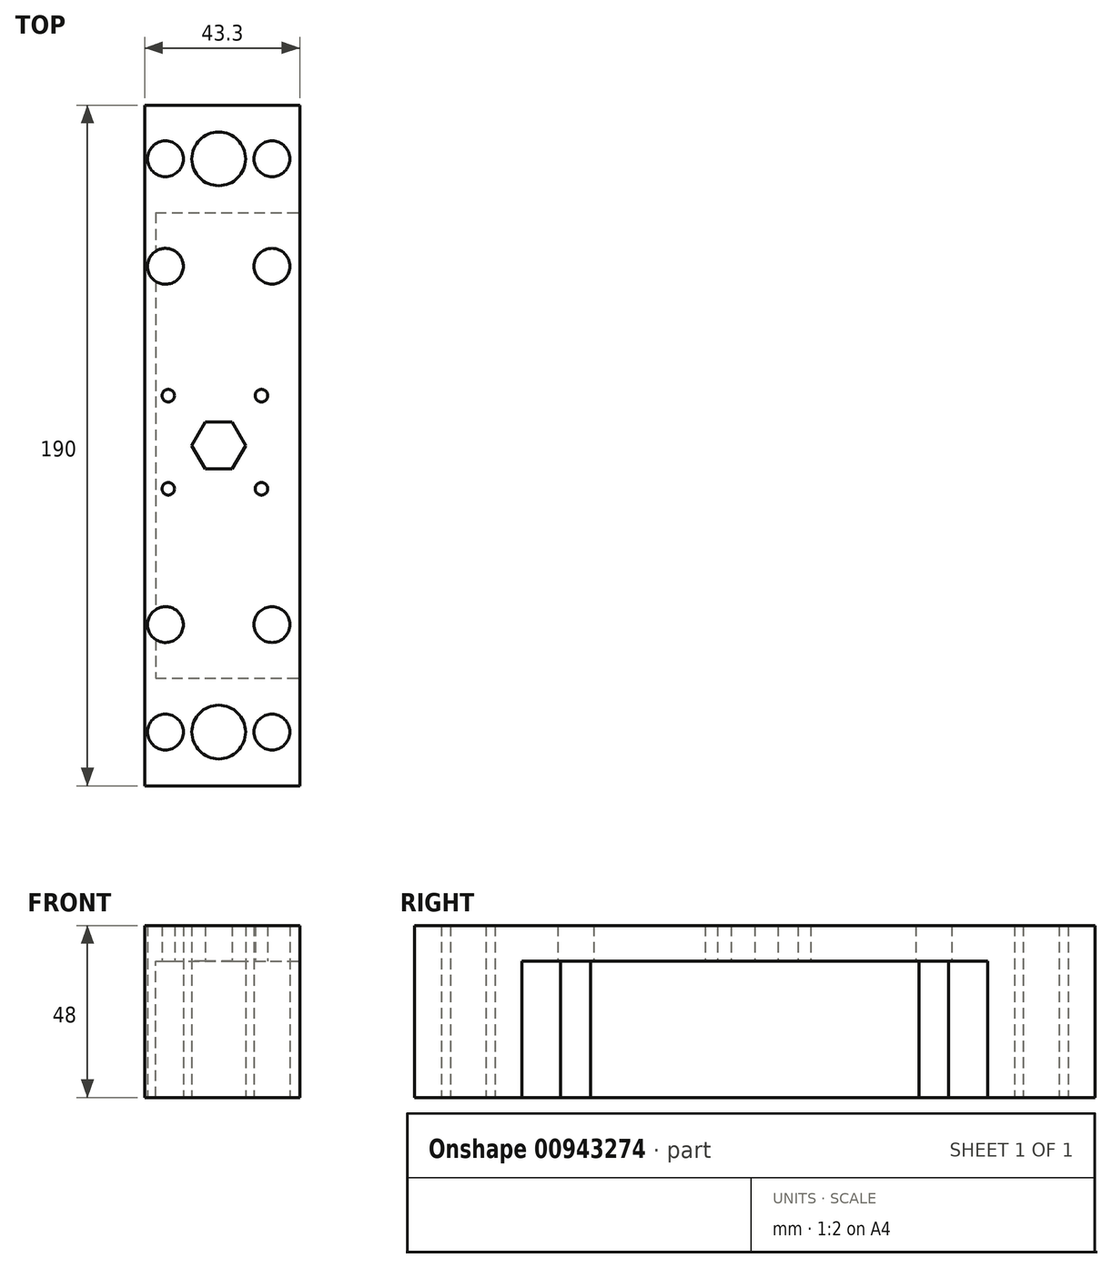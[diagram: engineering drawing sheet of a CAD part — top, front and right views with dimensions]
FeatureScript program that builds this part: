
annotation { "Feature Type Name" : "Feature", "Feature Type Description" : "" }
export const myFeature = defineFeature(function(context is Context, id is Id, definition is map)
    precondition{}
    {
        {
            var Q0;
            Q0=qCreatedBy(makeId("Top.planeOp"),FACE);
            var sketch = newSketch(context, id + "F0", { "sketchPlane" : qUnion([Q0])});
            skCircle(sketch, "E0", {"center": v(11.93, 13.9) * mm, "radius": 1.75 * mm});
            skCircle(sketch, "E1.MirrorC", {"center": v(-14.07, -12.1) * mm, "radius": 1.75 * mm});
            skCircle(sketch, "E2.MirrorC", {"center": v(11.93, -12.1) * mm, "radius": 1.75 * mm});
            skCircle(sketch, "E3.MirrorC", {"center": v(-14.07, 13.9) * mm, "radius": 1.75 * mm});
            skLineSegment(sketch, "E4", {"start": v(-20.65, 17.6) * mm, "end": v(-20.65, -17.6) * mm});
            skLineSegment(sketch, "E5", {"start": v(30.65, 0) * mm, "end": v(30.65, -95) * mm});
            skLineSegment(sketch, "E6", {"start": v(-20.65, 0) * mm, "end": v(-20.65, -95) * mm});
            skLineSegment(sketch, "E7", {"start": v(30.65, -95) * mm, "end": v(-20.65, -95) * mm});
            skLineSegment(sketch, "E8", {"start": v(0, 0) * mm, "end": v(0, -80) * mm, "construction": true});
            skCircle(sketch, "E9", {"center": v(0, -80) * mm, "radius": 7.5 * mm});
            skLineSegment(sketch, "E10.MirrorCS", {"start": v(30.65, 0) * mm, "end": v(30.65, 95) * mm});
            skLineSegment(sketch, "E11.MirrorCS", {"start": v(-20.65, 0) * mm, "end": v(-20.65, 95) * mm});
            skLineSegment(sketch, "E12.MirrorCS", {"start": v(30.65, 95) * mm, "end": v(-20.65, 95) * mm});
            skLineSegment(sketch, "E13", {"start": v(0, -80) * mm, "end": v(-20.65, -80) * mm, "construction": true});
            skCircle(sketch, "E14", {"center": v(-14.88, -80) * mm, "radius": 1.4 * mm});
            skCircle(sketch, "E15", {"center": v(-14.88, -80) * mm, "radius": 5 * mm});
            skCircle(sketch, "E16.MirrorC", {"center": v(14.88, -80) * mm, "radius": 5 * mm});
            skCircle(sketch, "E17.MirrorC", {"center": v(14.88, -80) * mm, "radius": 1.4 * mm});
            skCircle(sketch, "E18.0.1.0", {"center": v(14.88, -50) * mm, "radius": 5 * mm});
            skLineSegment(sketch, "E18.direction2", {"start": v(14.88, -80) * mm, "end": v(14.88, -50) * mm, "construction": true});
            skCircle(sketch, "E19.0.1.0", {"center": v(14.88, -50) * mm, "radius": 1.4 * mm});
            skCircle(sketch, "E20.MirrorC", {"center": v(-14.88, -50) * mm, "radius": 5 * mm});
            skCircle(sketch, "E21", {"center": v(-14.88, -50) * mm, "radius": 1.4 * mm});
            skCircle(sketch, "E22.MirrorC", {"center": v(-14.88, 50) * mm, "radius": 5 * mm});
            skCircle(sketch, "E23.MirrorC", {"center": v(-14.88, 50) * mm, "radius": 1.4 * mm});
            skCircle(sketch, "E24.MirrorC", {"center": v(14.88, 50) * mm, "radius": 5 * mm});
            skCircle(sketch, "E25.MirrorC", {"center": v(14.88, 50) * mm, "radius": 1.4 * mm});
            skCircle(sketch, "E26.MirrorC", {"center": v(14.88, 80) * mm, "radius": 5 * mm});
            skCircle(sketch, "E27.MirrorC", {"center": v(14.88, 80) * mm, "radius": 1.4 * mm});
            skCircle(sketch, "E28.MirrorC", {"center": v(0, 80) * mm, "radius": 7.5 * mm});
            skCircle(sketch, "E29.MirrorC", {"center": v(-14.88, 80) * mm, "radius": 5 * mm});
            skCircle(sketch, "E30.MirrorC", {"center": v(-14.88, 80) * mm, "radius": 1.4 * mm});
            skLineSegment(sketch, "E31", {"start": v(0, 80) * mm, "end": v(0, 0) * mm, "construction": true});
            skLineSegment(sketch, "E32", {"start": v(0, 80) * mm, "end": v(-14.88, 80) * mm, "construction": true});
            skSolve(sketch);
        }
        {
            var Q0;
            Q0=makeQuery(id+"F0.imprint","IMPRINT",FACE,{"disambiguationData":[TD([[makeQuery(id+"F0.imprint","IMPRINT",EDGE,{"derivedFrom":sQuery(id+"F0.wireOp",EDGE,"E0")}),-1.0]])]});
            var sketch = newSketch(context, id + "F1", { "sketchPlane" : qUnion([Q0])});
            skLineSegment(sketch, "E33.bottom", {"start": v(7, 10) * mm, "end": v(-7, 10) * mm});
            skLineSegment(sketch, "E33.top", {"start": v(7, -10) * mm, "end": v(-7, -10) * mm});
            skLineSegment(sketch, "E33.left", {"start": v(10, 7) * mm, "end": v(10, -7) * mm});
            skLineSegment(sketch, "E33.right", {"start": v(-10, 7) * mm, "end": v(-10, -7) * mm});
            skPoint(sketch, "E33.middle", {"position": v(0, 0) * mm});
            skCircle(sketch, "E34.cCircle", {"center": v(0, 0) * mm, "radius": 6.55 * mm, "construction": true});
            skLineSegment(sketch, "E34.0", {"start": v(-3.78, 6.55) * mm, "end": v(3.78, 6.55) * mm});
            skLineSegment(sketch, "E34.1", {"start": v(3.78, 6.55) * mm, "end": v(7.56, 0) * mm});
            skLineSegment(sketch, "E34.2", {"start": v(7.56, 0) * mm, "end": v(3.78, -6.55) * mm});
            skLineSegment(sketch, "E34.3", {"start": v(3.78, -6.55) * mm, "end": v(-3.78, -6.55) * mm});
            skLineSegment(sketch, "E34.4", {"start": v(-3.78, -6.55) * mm, "end": v(-7.56, 0) * mm});
            skLineSegment(sketch, "E34.5", {"start": v(-7.56, 0) * mm, "end": v(-3.78, 6.55) * mm});
            skPoint(sketch, "E34.0.midPoint", {"position": v(0, 6.55) * mm});
            skPoint(sketch, "E35.visualSharp", {"position": v(-10, 10) * mm});
            skArc(sketch, "E35.filletArc", {"start": v(-7, 10) * mm, "mid": v(-9.12, 9.12) * mm, "end": v(-10, 7) * mm});
            skPoint(sketch, "E36.visualSharp", {"position": v(10, 10) * mm});
            skArc(sketch, "E36.filletArc", {"start": v(10, 7) * mm, "mid": v(9.12, 9.12) * mm, "end": v(7, 10) * mm});
            skPoint(sketch, "E37.visualSharp", {"position": v(10, -10) * mm});
            skArc(sketch, "E37.filletArc", {"start": v(7, -10) * mm, "mid": v(9.12, -9.12) * mm, "end": v(10, -7) * mm});
            skPoint(sketch, "E38.visualSharp", {"position": v(-10, -10) * mm});
            skArc(sketch, "E38.filletArc", {"start": v(-10, -7) * mm, "mid": v(-9.12, -9.12) * mm, "end": v(-7, -10) * mm});
            skSolve(sketch);
        }
        {
            var Q0;
            Q0=makeQuery(id+"F0.imprint","IMPRINT",FACE,{"disambiguationData":[TD([[makeQuery(id+"F0.imprint","IMPRINT",EDGE,{"derivedFrom":sQuery(id+"F0.wireOp",EDGE,"E0")}),-1.0]])]});
            extrude(context, id + "F2", {"entities" : qUnion([Q0]), "depth" : 48 * mm, "offsetDistance" : 25 * mm});
        }
        {
            var Q0;
            Q0=makeQuery(id+"F1.imprint","IMPRINT",FACE,{"disambiguationData":[TD([[makeQuery(id+"F1.imprint","IMPRINT",EDGE,{"derivedFrom":sQuery(id+"F1.wireOp",EDGE,"E34.0")}),-1.0]])]});
            extrude(context, id + "F3", {"entities" : qUnion([Q0]), "operationType" : NewBodyOperationType.REMOVE, "oppositeDirection" : true, "depth" : -48 * mm, "offsetDistance" : 25 * mm});
        }
        {
            var Q0;
            Q0=makeQuery(id+"F2.opExtrude","SWEPT_FACE",FACE,{"disambiguationData":[OSD([sQuery(id+"F0.wireOp",EDGE,"E5"),sQuery(id+"F0.wireOp",EDGE,"E10.MirrorCS")])]});
            var sketch = newSketch(context, id + "F4", { "sketchPlane" : qUnion([Q0])});
            skLineSegment(sketch, "E39", {"start": v(-95, 24) * mm, "end": v(-65, 24) * mm, "construction": true});
            skLineSegment(sketch, "E40.MirrorCS", {"start": v(95, 24) * mm, "end": v(65, 24) * mm, "construction": true});
            skLineSegment(sketch, "E41.bottom", {"start": v(-65, 0) * mm, "end": v(65, 0) * mm});
            skLineSegment(sketch, "E41.top", {"start": v(-65, 38) * mm, "end": v(65, 38) * mm});
            skLineSegment(sketch, "E41.left", {"start": v(-65, 0) * mm, "end": v(-65, 38) * mm});
            skLineSegment(sketch, "E41.right", {"start": v(65, 0) * mm, "end": v(65, 38) * mm});
            skSolve(sketch);
        }
        {
            var Q0;
            Q0=makeQuery(id+"F4.imprint","IMPRINT",FACE,{"disambiguationData":[TD([[makeQuery(id+"F4.imprint","IMPRINT",EDGE,{"derivedFrom":sQuery(id+"F4.wireOp",EDGE,"E41.bottom")}),-1.0]])]});
            extrude(context, id + "F5", {"entities" : qUnion([Q0]), "operationType" : NewBodyOperationType.REMOVE, "oppositeDirection" : true, "depth" : 48.3 * mm, "offsetDistance" : 25 * mm});
        }
        {
            var Q0;
            Q0=makeQuery(id+"F2.opExtrude","CAP_FACE",FACE,{"disambiguationData":[OSD([sQuery(id+"F0.wireOp",EDGE,"E0"),sQuery(id+"F0.wireOp",EDGE,"E1.MirrorC"),sQuery(id+"F0.wireOp",EDGE,"E2.MirrorC"),sQuery(id+"F0.wireOp",EDGE,"E3.MirrorC"),sQuery(id+"F0.wireOp",EDGE,"E5"),sQuery(id+"F0.wireOp",EDGE,"E6"),sQuery(id+"F0.wireOp",EDGE,"E7"),sQuery(id+"F0.wireOp",EDGE,"E9"),sQuery(id+"F0.wireOp",EDGE,"E10.MirrorCS"),sQuery(id+"F0.wireOp",EDGE,"E11.MirrorCS"),sQuery(id+"F0.wireOp",EDGE,"E12.MirrorCS"),sQuery(id+"F0.wireOp",EDGE,"E15"),sQuery(id+"F0.wireOp",EDGE,"E16.MirrorC"),sQuery(id+"F0.wireOp",EDGE,"E18.0.1.0"),sQuery(id+"F0.wireOp",EDGE,"E20.MirrorC"),sQuery(id+"F0.wireOp",EDGE,"E22.MirrorC"),sQuery(id+"F0.wireOp",EDGE,"E24.MirrorC"),sQuery(id+"F0.wireOp",EDGE,"E26.MirrorC"),sQuery(id+"F0.wireOp",EDGE,"E28.MirrorC"),sQuery(id+"F0.wireOp",EDGE,"E29.MirrorC")])],"isStart":false});
            var sketch = newSketch(context, id + "F6", { "sketchPlane" : qUnion([Q0])});
            skLineSegment(sketch, "E42", {"start": v(30.65, -81.45) * mm, "end": v(22.65, -81.45) * mm, "construction": true});
            skLineSegment(sketch, "E43", {"start": v(22.65, -95) * mm, "end": v(22.65, 95) * mm});
            skSolve(sketch);
        }
        {
            var Q0;
            {var subQ0=sQuery(id+"F6.wireOp",EDGE,"E43");Q0=makeQuery(id+"F6.imprint","IMPRINT",FACE,{"disambiguationData":[TD([[makeQuery(id+"F6.imprint","IMPRINT",EDGE,{"derivedFrom":subQ0}),-1.0]])]});}
            extrude(context, id + "F7", {"entities" : qUnion([Q0]), "operationType" : NewBodyOperationType.REMOVE, "oppositeDirection" : true, "depth" : 50 * mm, "offsetDistance" : 25 * mm});
        }
    });
